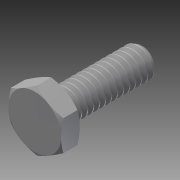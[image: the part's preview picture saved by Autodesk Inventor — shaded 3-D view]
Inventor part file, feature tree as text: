
AUTODESK INVENTOR PART (.ipt)
format: ipt  version: 2014 SP1 (Build 180222100, 222)  size: 567,296 bytes
history: native  units: in
note: dims shown in document units (in); Inventor stores cm internally (conversion verified against a paired STEP export)
features: extrude x1, other x1, imported_body x1
ambient origin geometry x8: Origin, YZ Plane, XZ Plane, XY Plane, X Axis, Y Axis, Z Axis, Center Point
bodies: Body1 (feature_tree)
feature tree (3):
  extrude  "Extrude14"  [1 undecoded]
  other  "92620A5401"
  imported_body  "Base1"
note: 1 required parameter value undecoded (feature->parameter linkage not recoverable at this tier; creation-order binding heuristic only, values carry confidence <= 0.55)
